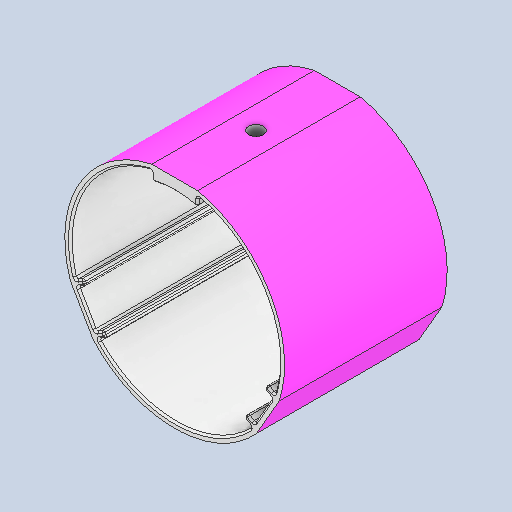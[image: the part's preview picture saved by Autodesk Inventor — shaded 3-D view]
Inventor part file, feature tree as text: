
AUTODESK INVENTOR PART (.ipt)
format: ipt  version: 2024.2 (Build 282272000, 272)  size: 209,408 bytes
history: native  units: in
note: dims shown in document units (in); Inventor stores cm internally (conversion verified against a paired STEP export)
features: chamfer x1
ambient origin geometry x8: Origin, YZ Plane, XZ Plane, XY Plane, X Axis, Y Axis, Z Axis, Center Point
bodies: Solid1 (feature_tree)
feature tree (1):
  chamfer  "Chamfer1"  [1 undecoded]
note: 1 required parameter value undecoded (feature->parameter linkage not recoverable at this tier; creation-order binding heuristic only, values carry confidence <= 0.55)
